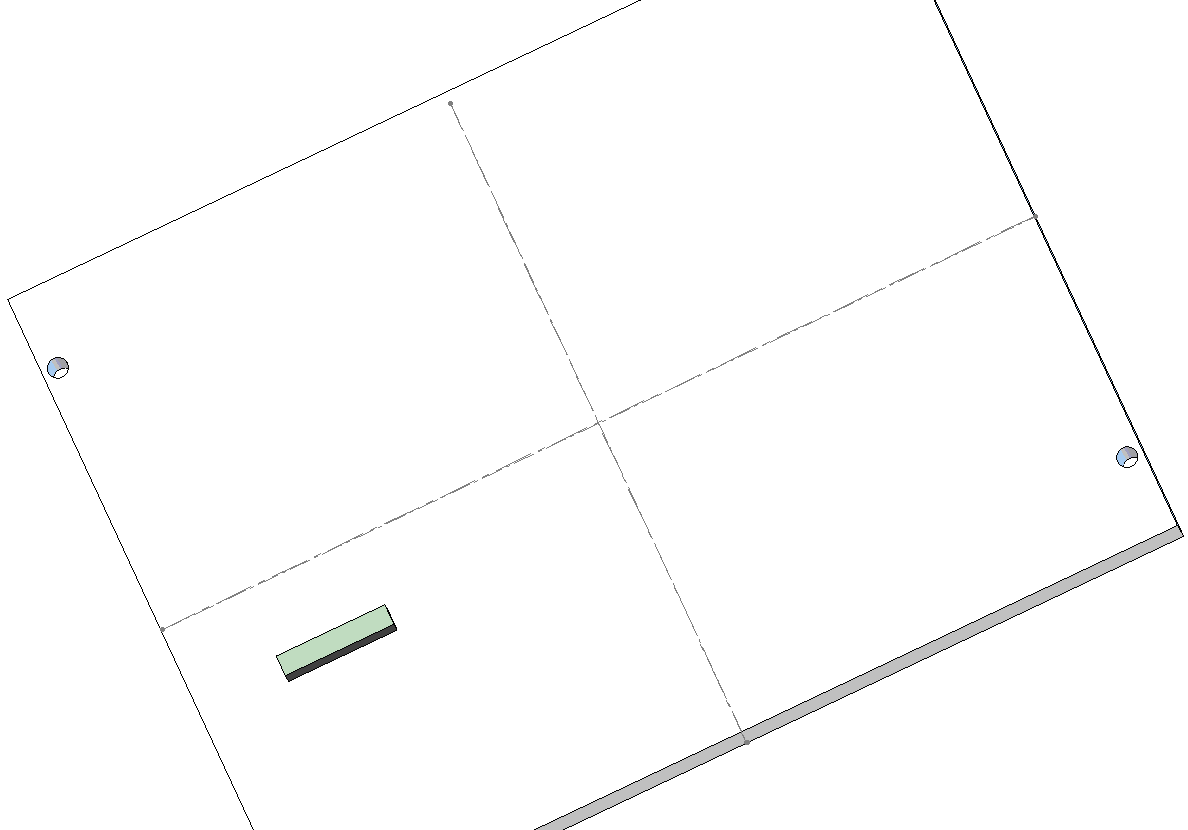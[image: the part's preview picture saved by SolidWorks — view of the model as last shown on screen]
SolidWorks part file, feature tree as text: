
SOLIDWORKS PART (.sldprt)
format: sldprt  version: not decoded by parser v0  size: 153,600 bytes
history: native  units: mm
features: sketch x5, extrude x2, cut_extrude x2, material x1 (+13 scaffold rows collapsed)
feature tree (23):
  scaffold x13  (default folders/planes/origin — collapsed)
  material  "Material <not specified>"
  sketch  "Sketch1"  dims[D1=158.0mm D2=120.36mm]
  extrude  "Extrude1"  Depth=7mm
  sketch  "Sketch2"  dims[D1=135.46mm D2=101.9mm D3=11.27mm D4=9.23mm]
  cut_extrude  "Bezel Opening"  Depth=0.1mm
  sketch  "Sketch3"  dims[c1.D1=1.25mm c1.D3=1.25mm c2.D1=3.5mm c2.D2=3.5mm c2.D3=3.5mm c2.D4=3.5mm c3.D2=1.8mm c3.D1=2.5mm c4.D2=1.8mm c4.D3=18.5mm c4.D5=91.9mm c4.D6=14.23mm c4.D7=2.75mm c4.D8=152.5mm]
  cut_extrude  "Mount hole cut"  Depth=10mm
  sketch  "Center lines"
  sketch  "Sketch4"  dims[D1=25.25mm D2=42.7mm]
  extrude  "Hirose DF9 connector"  Depth=3.75mm
decode coverage: 8 of 9 modeling features carry decoded parameters
note: suppression state not decoded; provenance and decode notes live in map.json
